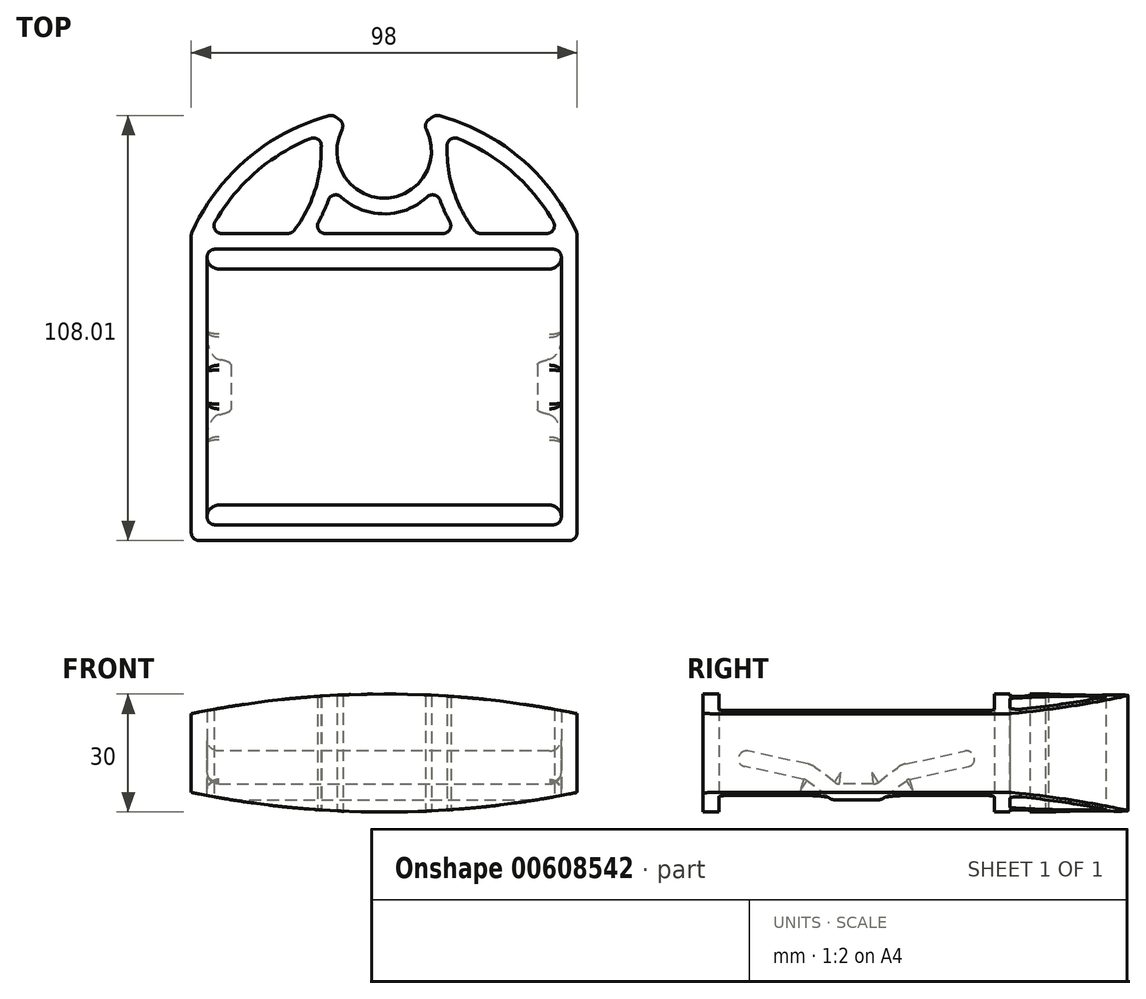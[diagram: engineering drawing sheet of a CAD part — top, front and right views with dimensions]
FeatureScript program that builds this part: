
annotation { "Feature Type Name" : "Feature", "Feature Type Description" : "" }
export const myFeature = defineFeature(function(context is Context, id is Id, definition is map)
    precondition{}
    {
        {
            var Q0;
            Q0=qCreatedBy(makeId("Top.planeOp"),FACE);
            var sketch = newSketch(context, id + "F0", { "sketchPlane" : qUnion([Q0])});
            skCircle(sketch, "E0", {"center": v(0, 0) * mm, "radius": 12 * mm});
            skSolve(sketch);
        }
        {
            var Q0;
            Q0=qCreatedBy(makeId("Top.planeOp"),FACE);
            var sketch = newSketch(context, id + "F1", { "sketchPlane" : qUnion([Q0])});
            skArc(sketch, "E1.0", {"start": v(-9.83, 6.88) * mm, "mid": v(-10.64, -5.54) * mm, "end": v(0, -12) * mm});
            skArc(sketch, "E2.0", {"start": v(-15.4, 4.36) * mm, "mid": v(-15.85, 2.2) * mm, "end": v(-16, 0) * mm});
            skLineSegment(sketch, "E3", {"start": v(0, -16) * mm, "end": v(0, -12) * mm});
            skLineSegment(sketch, "E4", {"start": v(0, 0) * mm, "end": v(0, -12) * mm, "construction": true});
            skPoint(sketch, "E5.orphan", {"position": v(0, 16) * mm});
            skLineSegment(sketch, "E6", {"start": v(-13.1, 9.18) * mm, "end": v(-9.83, 6.88) * mm});
            skLineSegment(sketch, "E7", {"start": v(0, 0) * mm, "end": v(-9.83, 6.88) * mm, "construction": true});
            skLineSegment(sketch, "E8", {"start": v(0, -16) * mm, "end": v(0, -21) * mm, "construction": true});
            skLineSegment(sketch, "E9", {"start": v(0, -21) * mm, "end": v(0, -25) * mm});
            skLineSegment(sketch, "E10", {"start": v(0, -21) * mm, "end": v(-18.54, -21) * mm});
            skLineSegment(sketch, "E11", {"start": v(0, -25) * mm, "end": v(-45, -25) * mm});
            skLineSegment(sketch, "E12", {"start": v(-49, -21) * mm, "end": v(-49, -99) * mm});
            skLineSegment(sketch, "E13", {"start": v(-45, -25) * mm, "end": v(-45, -95) * mm});
            skLineSegment(sketch, "E14", {"start": v(-45, -25) * mm, "end": v(-49, -25) * mm, "construction": true});
            skLineSegment(sketch, "E15", {"start": v(-45, -95) * mm, "end": v(0, -95) * mm});
            skLineSegment(sketch, "E16", {"start": v(0, -95) * mm, "end": v(0, -99) * mm});
            skLineSegment(sketch, "E17", {"start": v(0, -99) * mm, "end": v(-49, -99) * mm});
            skLineSegment(sketch, "E18", {"start": v(0, -25) * mm, "end": v(45, -25) * mm, "construction": true});
            skLineSegment(sketch, "E19", {"start": v(0, 0) * mm, "end": v(-12, 0) * mm, "construction": true});
            skArc(sketch, "E20", {"start": v(-13.1, 9.18) * mm, "mid": v(-34.52, -1.78) * mm, "end": v(-49, -21) * mm});
            skArc(sketch, "E21", {"start": v(-23.54, -21) * mm, "mid": v(-17.94, -11.16) * mm, "end": v(-16, 0) * mm});
            skArc(sketch, "E22", {"start": v(-18.54, -21) * mm, "mid": v(-15.31, -15.3) * mm, "end": v(-13.14, -9.12) * mm});
            skLineSegment(sketch, "E23", {"start": v(-17.94, -11.16) * mm, "end": v(-14.18, -12.5) * mm, "construction": true});
            skArc(sketch, "E24", {"start": v(-15.4, 4.36) * mm, "mid": v(-32.56, -5.36) * mm, "end": v(-44.58, -21) * mm});
            skLineSegment(sketch, "E25", {"start": v(-34.52, -1.78) * mm, "end": v(-31.95, -4.84) * mm, "construction": true});
            skArc(sketch, "E26.trimOffspring", {"start": v(-13.14, -9.12) * mm, "mid": v(-7.42, -14.18) * mm, "end": v(0, -16) * mm});
            skLineSegment(sketch, "E27.trimOffspring", {"start": v(-23.54, -21) * mm, "end": v(-44.58, -21) * mm});
            skSolve(sketch);
        }
        {
            var Q0;
            Q0=qSketchRegion(id+"F1",true);
            extrude(context, id + "F2", {"entities" : qUnion([Q0]), "depth" : 30 * mm});
        }
        {
            var Q0;
            Q0=qCreatedBy(makeId("Right.planeOp"),FACE);
            var sketch = newSketch(context, id + "F3", { "sketchPlane" : qUnion([Q0])});
            skLineSegment(sketch, "E28", {"start": v(-95, 0) * mm, "end": v(-25, 0) * mm, "construction": true});
            skLineSegment(sketch, "E29", {"start": v(-60, 0) * mm, "end": v(-60, 30) * mm, "construction": true});
            skLineSegment(sketch, "E30", {"start": v(-95, 17.08) * mm, "end": v(-71.27, 11.98) * mm});
            skLineSegment(sketch, "E31", {"start": v(-71.27, 11.98) * mm, "end": v(-65, 7.14) * mm});
            skLineSegment(sketch, "E32.0", {"start": v(-73, 8.26) * mm, "end": v(-66.36, 3.14) * mm});
            skLineSegment(sketch, "E32.1", {"start": v(-95, 13) * mm, "end": v(-73, 8.26) * mm});
            skLineSegment(sketch, "E33", {"start": v(-95, 13) * mm, "end": v(-95, 17.08) * mm});
            skLineSegment(sketch, "E34.MirrorCS", {"start": v(-25, 13) * mm, "end": v(-47, 8.26) * mm});
            skLineSegment(sketch, "E35.MirrorCS", {"start": v(-25, 13) * mm, "end": v(-25, 17.08) * mm});
            skLineSegment(sketch, "E36.MirrorCS", {"start": v(-25, 17.08) * mm, "end": v(-48.73, 11.98) * mm});
            skLineSegment(sketch, "E37.MirrorCS", {"start": v(-48.73, 11.98) * mm, "end": v(-55, 7.14) * mm});
            skLineSegment(sketch, "E38.MirrorCS", {"start": v(-47, 8.26) * mm, "end": v(-53.64, 3.14) * mm});
            skLineSegment(sketch, "E39", {"start": v(-65, 7.14) * mm, "end": v(-55, 7.14) * mm});
            skLineSegment(sketch, "E40", {"start": v(-66.36, 3.14) * mm, "end": v(-53.64, 3.14) * mm});
            skLineSegment(sketch, "E41", {"start": v(-65, 7.14) * mm, "end": v(-65, 3.14) * mm, "construction": true});
            skSolve(sketch);
        }
        {
            var Q0;
            Q0=qSketchRegion(id+"F3",true);
            extrude(context, id + "F4", {"entities" : qUnion([Q0]), "operationType" : NewBodyOperationType.ADD, "endBound" : BoundingType.UP_TO_NEXT, "oppositeDirection" : true, "depth" : 25 * mm});
        }
        {
            var Q0;
            Q0=qCreatedBy(makeId("Top.planeOp"),FACE);
            var sketch = newSketch(context, id + "F5", { "sketchPlane" : qUnion([Q0])});
            skLineSegment(sketch, "E42.bottom", {"start": v(-45, -25) * mm, "end": v(0, -25) * mm});
            skLineSegment(sketch, "E42.top", {"start": v(-45, -30) * mm, "end": v(0, -30) * mm});
            skLineSegment(sketch, "E42.left", {"start": v(-45, -25) * mm, "end": v(-45, -30) * mm});
            skLineSegment(sketch, "E42.right", {"start": v(0, -25) * mm, "end": v(0, -30) * mm});
            skLineSegment(sketch, "E43.bottom", {"start": v(-45, -95) * mm, "end": v(0, -95) * mm});
            skLineSegment(sketch, "E43.top", {"start": v(-45, -90) * mm, "end": v(0, -90) * mm});
            skLineSegment(sketch, "E43.left", {"start": v(-45, -95) * mm, "end": v(-45, -90) * mm});
            skLineSegment(sketch, "E43.right", {"start": v(0, -95) * mm, "end": v(0, -90) * mm});
            skSolve(sketch);
        }
        {
            var Q0;
            Q0=qSketchRegion(id+"F5",true);
            extrude(context, id + "F6", {"entities" : qUnion([Q0]), "operationType" : NewBodyOperationType.REMOVE, "endBound" : BoundingType.THROUGH_ALL, "depth" : 25 * mm});
        }
        {
            var Q0;
            Q0=makeQuery(id+"F2.opExtrude","SWEPT_EDGE",EDGE,{"disambiguationData":[OSD([sQuery(id+"F1.wireOp",EDGE,"E11"),sQuery(id+"F1.wireOp",EDGE,"E13")])]});
            var Q1;
            Q1=makeQuery(id+"F2.opExtrude","SWEPT_EDGE",EDGE,{"disambiguationData":[OSD([sQuery(id+"F1.wireOp",EDGE,"E13"),sQuery(id+"F1.wireOp",EDGE,"E15")])]});
            var Q2;
            Q2=makeQuery(id+"F2.opExtrude","SWEPT_EDGE",EDGE,{"disambiguationData":[OSD([sQuery(id+"F1.wireOp",EDGE,"E6"),sQuery(id+"F1.wireOp",EDGE,"E20")])]});
            var Q3;
            Q3=makeQuery(id+"F2.opExtrude","SWEPT_EDGE",EDGE,{"disambiguationData":[OSD([sQuery(id+"F1.wireOp",EDGE,"E1.0"),sQuery(id+"F1.wireOp",EDGE,"E6")])]});
            var Q4;
            Q4=makeQuery(id+"F2.opExtrude","SWEPT_EDGE",EDGE,{"disambiguationData":[OSD([sQuery(id+"F1.wireOp",EDGE,"E12"),sQuery(id+"F1.wireOp",EDGE,"E20")])]});
            var Q5;
            Q5=makeQuery(id+"F2.opExtrude","SWEPT_EDGE",EDGE,{"disambiguationData":[OSD([sQuery(id+"F1.wireOp",EDGE,"E12"),sQuery(id+"F1.wireOp",EDGE,"E17")])]});
            var Q6;
            Q6=makeQuery(id+"F2.opExtrude","SWEPT_EDGE",EDGE,{"disambiguationData":[OSD([sQuery(id+"F1.wireOp",EDGE,"E21"),sQuery(id+"F1.wireOp",EDGE,"E27.trimOffspring")])]});
            var Q7;
            Q7=makeQuery(id+"F2.opExtrude","SWEPT_EDGE",EDGE,{"disambiguationData":[OSD([sQuery(id+"F1.wireOp",EDGE,"E2.0"),sQuery(id+"F1.wireOp",EDGE,"E24")])]});
            var Q8;
            Q8=makeQuery(id+"F2.opExtrude","SWEPT_EDGE",EDGE,{"disambiguationData":[OSD([sQuery(id+"F1.wireOp",EDGE,"E22"),sQuery(id+"F1.wireOp",EDGE,"E26.trimOffspring")])]});
            var Q9;
            Q9=makeQuery(id+"F2.opExtrude","SWEPT_EDGE",EDGE,{"disambiguationData":[OSD([sQuery(id+"F1.wireOp",EDGE,"E10"),sQuery(id+"F1.wireOp",EDGE,"E22")])]});
            var Q10;
            Q10=makeQuery(id+"F2.opExtrude","SWEPT_EDGE",EDGE,{"disambiguationData":[OSD([sQuery(id+"F1.wireOp",EDGE,"E24"),sQuery(id+"F1.wireOp",EDGE,"E27.trimOffspring")])]});
            fillet(context, id + "F7", {"entities" : qUnion([Q0, Q1, Q2, Q3, Q4, Q5, Q6, Q7, Q8, Q9, Q10]), "radius" : 2 * mm, "tangentPropagation" : true, "allowEdgeOverflow" : false});
        }
        {
            var Q0;
            Q0=makeQuery(id+"F4.opExtrude","SWEPT_EDGE",EDGE,{"disambiguationData":[OSD([sQuery(id+"F3.wireOp",EDGE,"E36.MirrorCS"),sQuery(id+"F3.wireOp",EDGE,"E37.MirrorCS")])]});
            var Q1;
            Q1=makeQuery(id+"F4.opExtrude","SWEPT_EDGE",EDGE,{"disambiguationData":[OSD([sQuery(id+"F3.wireOp",EDGE,"E30"),sQuery(id+"F3.wireOp",EDGE,"E31")])]});
            fillet(context, id + "F8", {"entities" : qUnion([Q0, Q1]), "radius" : 5 * mm, "tangentPropagation" : true, "allowEdgeOverflow" : false});
        }
        {
            var Q0;
            Q0=makeQuery(id+"F4.opExtrude","SWEPT_EDGE",EDGE,{"disambiguationData":[OSD([sQuery(id+"F3.wireOp",EDGE,"E32.0"),sQuery(id+"F3.wireOp",EDGE,"E32.1")])]});
            fillet(context, id + "F9", {"entities" : qUnion([Q0]), "radius" : 2 * mm, "tangentPropagation" : true, "allowEdgeOverflow" : false});
        }
        {
            var Q0;
            Q0=makeQuery(id+"F4.opExtrude","SWEPT_EDGE",EDGE,{"disambiguationData":[OSD([sQuery(id+"F3.wireOp",EDGE,"E34.MirrorCS"),sQuery(id+"F3.wireOp",EDGE,"E38.MirrorCS")])]});
            var Q1;
            Q1=makeQuery(id+"F4.opExtrude","SWEPT_EDGE",EDGE,{"disambiguationData":[OSD([sQuery(id+"F3.wireOp",EDGE,"E32.0"),sQuery(id+"F3.wireOp",EDGE,"IAGzdYc4-z68C-EQy4-V6Kw-QF0httY63qSp")])]});
            var Q2;
            Q2=makeQuery(id+"F4.opExtrude","SWEPT_EDGE",EDGE,{"disambiguationData":[OSD([sQuery(id+"F3.wireOp",EDGE,"E31"),sQuery(id+"F3.wireOp",EDGE,"IAGzdYc4-z68C-EQy4-V6Kw-QF0httY63qSp")])]});
            var Q3;
            Q3=makeQuery(id+"F4.opExtrude","SWEPT_EDGE",EDGE,{"disambiguationData":[OSD([sQuery(id+"F3.wireOp",EDGE,"E38.MirrorCS"),sQuery(id+"F3.wireOp",EDGE,"90d33c85-e0a6-49d1-bc45-df9b89ce86660.MirrorCS")])]});
            var Q4;
            Q4=makeQuery(id+"F4.opExtrude","SWEPT_EDGE",EDGE,{"disambiguationData":[OSD([sQuery(id+"F3.wireOp",EDGE,"E37.MirrorCS"),sQuery(id+"F3.wireOp",EDGE,"90d33c85-e0a6-49d1-bc45-df9b89ce86660.MirrorCS")])]});
            var Q5;
            Q5=makeQuery(id+"F6.boolean.opBoolean","INTERSECT",EDGE,{"derivedFrom":[makeQuery(id+"F4.opExtrude","SWEPT_FACE",FACE,{"disambiguationData":[OSD([sQuery(id+"F3.wireOp",EDGE,"E30")])]}),makeQuery(id+"F6.opExtrude","SWEPT_FACE",FACE,{"disambiguationData":[OSD([sQuery(id+"F5.wireOp",EDGE,"E43.top")])]})]});
            var Q6;
            Q6=makeQuery(id+"F6.boolean.opBoolean","INTERSECT",EDGE,{"derivedFrom":[makeQuery(id+"F4.opExtrude","SWEPT_FACE",FACE,{"disambiguationData":[OSD([sQuery(id+"F3.wireOp",EDGE,"E32.1")])]}),makeQuery(id+"F6.opExtrude","SWEPT_FACE",FACE,{"disambiguationData":[OSD([sQuery(id+"F5.wireOp",EDGE,"E43.top")])]})]});
            var Q7;
            Q7=makeQuery(id+"F6.boolean.opBoolean","INTERSECT",EDGE,{"derivedFrom":[makeQuery(id+"F4.opExtrude","SWEPT_FACE",FACE,{"disambiguationData":[OSD([sQuery(id+"F3.wireOp",EDGE,"E36.MirrorCS")])]}),makeQuery(id+"F6.opExtrude","SWEPT_FACE",FACE,{"disambiguationData":[OSD([sQuery(id+"F5.wireOp",EDGE,"E42.top")])]})]});
            var Q8;
            Q8=makeQuery(id+"F6.boolean.opBoolean","INTERSECT",EDGE,{"derivedFrom":[makeQuery(id+"F4.opExtrude","SWEPT_FACE",FACE,{"disambiguationData":[OSD([sQuery(id+"F3.wireOp",EDGE,"E34.MirrorCS")])]}),makeQuery(id+"F6.opExtrude","SWEPT_FACE",FACE,{"disambiguationData":[OSD([sQuery(id+"F5.wireOp",EDGE,"E42.top")])]})]});
            fillet(context, id + "F10", {"entities" : qUnion([Q0, Q1, Q2, Q3, Q4, Q5, Q6, Q7, Q8]), "radius" : 2 * mm, "tangentPropagation" : true, "allowEdgeOverflow" : false});
        }
        {
            var Q0;
            Q0=makeQuery(id+"F4.opExtrude","SWEPT_EDGE",EDGE,{"disambiguationData":[OSD([sQuery(id+"F3.wireOp",EDGE,"E35.MirrorCS"),sQuery(id+"F3.wireOp",EDGE,"E36.MirrorCS")])]});
            var Q1;
            Q1=makeQuery(id+"F4.opExtrude","TWEAK_EDGE",EDGE,{"derivedFrom":[makeQuery(id+"F2.opExtrude","SWEPT_FACE",FACE,{"disambiguationData":[OSD([sQuery(id+"F1.wireOp",EDGE,"E13")])]}),makeQuery(id+"F3.imprint","IMPRINT",EDGE,{"derivedFrom":sQuery(id+"F3.wireOp",EDGE,"E30")})]});
            var Q2;
            Q2=makeQuery(id+"F10.opFillet","BLEND_EDGE",EDGE,{"blendedFrom":[makeQuery(id+"F4.opExtrude","SWEPT_EDGE",EDGE,{"disambiguationData":[OSD([sQuery(id+"F3.wireOp",EDGE,"E38.MirrorCS"),sQuery(id+"F3.wireOp",EDGE,"90d33c85-e0a6-49d1-bc45-df9b89ce86660.MirrorCS")])]}),makeQuery(id+"F6.boolean.opBoolean","MERGE",FACE,{"derivedFrom":[makeQuery(id+"F2.opExtrude","SWEPT_FACE",FACE,{"disambiguationData":[OSD([sQuery(id+"F1.wireOp",EDGE,"E13")])]}),makeQuery(id+"F6.opExtrude","SWEPT_FACE",FACE,{"disambiguationData":[OSD([sQuery(id+"F5.wireOp",EDGE,"E42.left")])]}),makeQuery(id+"F6.opExtrude","SWEPT_FACE",FACE,{"disambiguationData":[OSD([sQuery(id+"F5.wireOp",EDGE,"E43.left")])]})]})],"blendedInto":[makeQuery(id+"F6.boolean.opBoolean","MERGE",FACE,{"derivedFrom":[makeQuery(id+"F2.opExtrude","SWEPT_FACE",FACE,{"disambiguationData":[OSD([sQuery(id+"F1.wireOp",EDGE,"E13")])]}),makeQuery(id+"F6.opExtrude","SWEPT_FACE",FACE,{"disambiguationData":[OSD([sQuery(id+"F5.wireOp",EDGE,"E42.left")])]}),makeQuery(id+"F6.opExtrude","SWEPT_FACE",FACE,{"disambiguationData":[OSD([sQuery(id+"F5.wireOp",EDGE,"E43.left")])]})]})]});
            fillet(context, id + "F11", {"entities" : qUnion([Q0, Q1, Q2]), "radius" : 3 * mm, "tangentPropagation" : true, "allowEdgeOverflow" : false});
        }
        {
            var Q0;
            Q0=makeQuery(id+"F2.opExtrude","SWEPT_FACE",FACE,{"disambiguationData":[OSD([sQuery(id+"F1.wireOp",EDGE,"E17")])]});
            var sketch = newSketch(context, id + "F12", { "sketchPlane" : qUnion([Q0])});
            skArc(sketch, "E44", {"start": v(0, 30) * mm, "mid": v(-24.63, 28.75) * mm, "end": v(-49, 25) * mm});
            skLineSegment(sketch, "E45", {"start": v(0, 30) * mm, "end": v(-49, 30) * mm});
            skLineSegment(sketch, "E46", {"start": v(-49, 25) * mm, "end": v(-49, 30) * mm});
            skLineSegment(sketch, "E47", {"start": v(0, 15) * mm, "end": v(-50.15, 15) * mm, "construction": true});
            skArc(sketch, "E48.MirrorCS", {"start": v(0, 0) * mm, "mid": v(-24.63, 1.25) * mm, "end": v(-49, 5) * mm});
            skLineSegment(sketch, "E49.MirrorCS", {"start": v(-49, 5) * mm, "end": v(-49, 0) * mm});
            skLineSegment(sketch, "E50.MirrorCS", {"start": v(0, 0) * mm, "end": v(-49, 0) * mm});
            skSolve(sketch);
        }
        {
            var Q0;
            Q0=qSketchRegion(id+"F12",true);
            extrude(context, id + "F13", {"entities" : qUnion([Q0]), "operationType" : NewBodyOperationType.REMOVE, "endBound" : BoundingType.THROUGH_ALL, "oppositeDirection" : true, "depth" : 25 * mm});
        }
        {
            var Q0;
            Q0=makeQuery(id+"F2.opExtrude","SWEPT_BODY",BODY,{"disambiguationData":[OSD([sQuery(id+"F1.wireOp",EDGE,"E1.0"),sQuery(id+"F1.wireOp",EDGE,"E2.0"),sQuery(id+"F1.wireOp",EDGE,"E3"),sQuery(id+"F1.wireOp",EDGE,"E6"),sQuery(id+"F1.wireOp",EDGE,"E9"),sQuery(id+"F1.wireOp",EDGE,"E10"),sQuery(id+"F1.wireOp",EDGE,"E11"),sQuery(id+"F1.wireOp",EDGE,"E12"),sQuery(id+"F1.wireOp",EDGE,"E13"),sQuery(id+"F1.wireOp",EDGE,"E15"),sQuery(id+"F1.wireOp",EDGE,"E16"),sQuery(id+"F1.wireOp",EDGE,"E17"),sQuery(id+"F1.wireOp",EDGE,"E20"),sQuery(id+"F1.wireOp",EDGE,"E21"),sQuery(id+"F1.wireOp",EDGE,"E22"),sQuery(id+"F1.wireOp",EDGE,"E24"),sQuery(id+"F1.wireOp",EDGE,"E26.trimOffspring"),sQuery(id+"F1.wireOp",EDGE,"E27.trimOffspring")])]});
            var Q1;
            Q1=qCreatedBy(makeId("Right.planeOp"),FACE);
            mirror(context, id + "F14", {"operationType" : NewBodyOperationType.ADD, "entities" : qUnion([Q0]), "mirrorPlane" : qUnion([Q1])});
        }
    });
